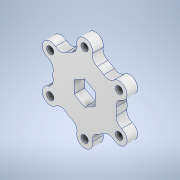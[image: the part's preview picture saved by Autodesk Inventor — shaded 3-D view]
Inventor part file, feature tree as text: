
AUTODESK INVENTOR PART (.ipt)
format: ipt  version: 2020 (Build 240168000, 168)  size: 204,800 bytes
history: native  units: in
note: dims shown in document units (in); Inventor stores cm internally (conversion verified against a paired STEP export)
features: extrude x1, sketch x1
ambient origin geometry x8: Origin, YZ Plane, XZ Plane, XY Plane, X Axis, Y Axis, Z Axis, Center Point
bodies: Solid1 (feature_tree)
feature tree (2):
  extrude  "Extrusion1"  Depth=0.9375in
  sketch  "Sketch1"  dims[d0=0.5in d1=0.17in d2=1.5in d3=0.375in d4=2.3622in d6=360.0deg d8=0.25in d9=0.0in d11=0.9375in d12=2.3622in d14=360.0deg]
